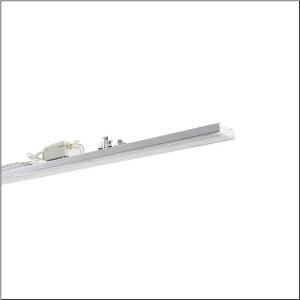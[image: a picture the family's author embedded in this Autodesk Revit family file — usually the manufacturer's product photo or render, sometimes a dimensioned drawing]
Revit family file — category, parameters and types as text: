
# Revit family: licross_11_recessed_ho_51te1edn4d5s
name_source: partatom
category: Lighting Fixtures
units: mm (PartAtom-declared; Revit-internal decimal feet)

## family parameters
Cut with Voids When Loaded = No
Host = Face
Light Source = No
Part Type = Normal
Room Calculation Point = No
Round Connector Dimension = Use Diameter
Shared = No

## types (1)
- --- (1 x LED, 13670 lm, 76.8 W, 4000K)
    Apparent Load = 77 VA
    CIE Flux Codes = 85 95 99 100 100
    Color Rendering = 80
    Color Temperature = 4000K
    Default Elevation = 1800 mm
    Description = Licross 11 Recessed HO, luminaire insert, of sheet steel, galvanised, coil coated, white, length: 1.500mm, width: 66mm, height: 67mm, LED rated luminous flux: 13.670lm, light colour: 840, SDCM (Standard Deviation of Colour Matching)MacAdam ≤ 2 SDCM (initial), control gear: DALI 2, with plug, 5-pole, with phase selection, mains connection: 220..240V, AC, 50/60Hz, rated input power: 77W, internal wiring halogen-free, primary light control with lens, of plastic, primary optical cover: cover, of PMMA, light emission: direct distribution, primary light characteristic: symmetric, protection rating (complete): IP54, insulation class (complete): insulation class I (protective earthing), certification: CE, ENEC, VDE, UKCA, protection symbol: D if used in an environment with non-conductive dust loads with corresponding accessories, impact resistance: IK06, permissible ambient temperature for indoor applications: -25..+30°C, corresponds to IFS (International Featured Standards) requirements for safety and quality in the food industry, reducing of maximum allowable ambient temperature of 5°C with ceiling mounting, LABS conformity tested according to VDMA 24364:2018-05, The light source and the operating device comply with the requirements of the Ecodesign Regulation (EU) 2019/2020 and are replaceable in accordance with this regulation, packaging unit: 1 piece
    Height = 58 mm
    Lamp = 1 x LED
    Lamp Light Flux = 13670 lm
    Lamp Power = 76.8 W
    Lamp count = 1
    Length = 1500 mm
    Luminous efficacy = 178 lm/W
    Manufacturer = Siteco
    ModVariant = No
    Model = 51TE1EDN4D5S
    Mounting Place = Ceiling
    Mounting Type = Pendant
    Number of Poles = 1
    OnlyDefault = Yes
    Power Factor = 1
    Product Name = Licross 11 Recessed HO
    Product group = luminaire insert | ceiling pendant
    ProductGroupID = 901
    Protection Class = Protection class I
    Protection Degree = IP 54
    RLX_Detail_Level = 1
    RLX_Emergency_Light_Flux = 0 lm
    RLX_Emergency_Type = 0
    RLX_Emergency_Type_DB = No
    RlxData = <blob elided: 24965 chars, md5=42a6fa70>
    Socket = socket
    Standby Power = 0 W
    System Light Flux = 13670 lm
    System Power = 77 W
    Type Comments = factory setting: luminous flux: 100 % | dim-lin: 254 | 522 mA
    Type Image = l_1296930.jpg
    URL = http://relux.com
    VarID = @adj_101369
    Voltage = 0 V
    Weight = 0.00 kg
    Width = 66 mm

## geometry (parser evidence)
native form markers: Blend x4, Sweep x12
no freeform markers — native parametric forms only
